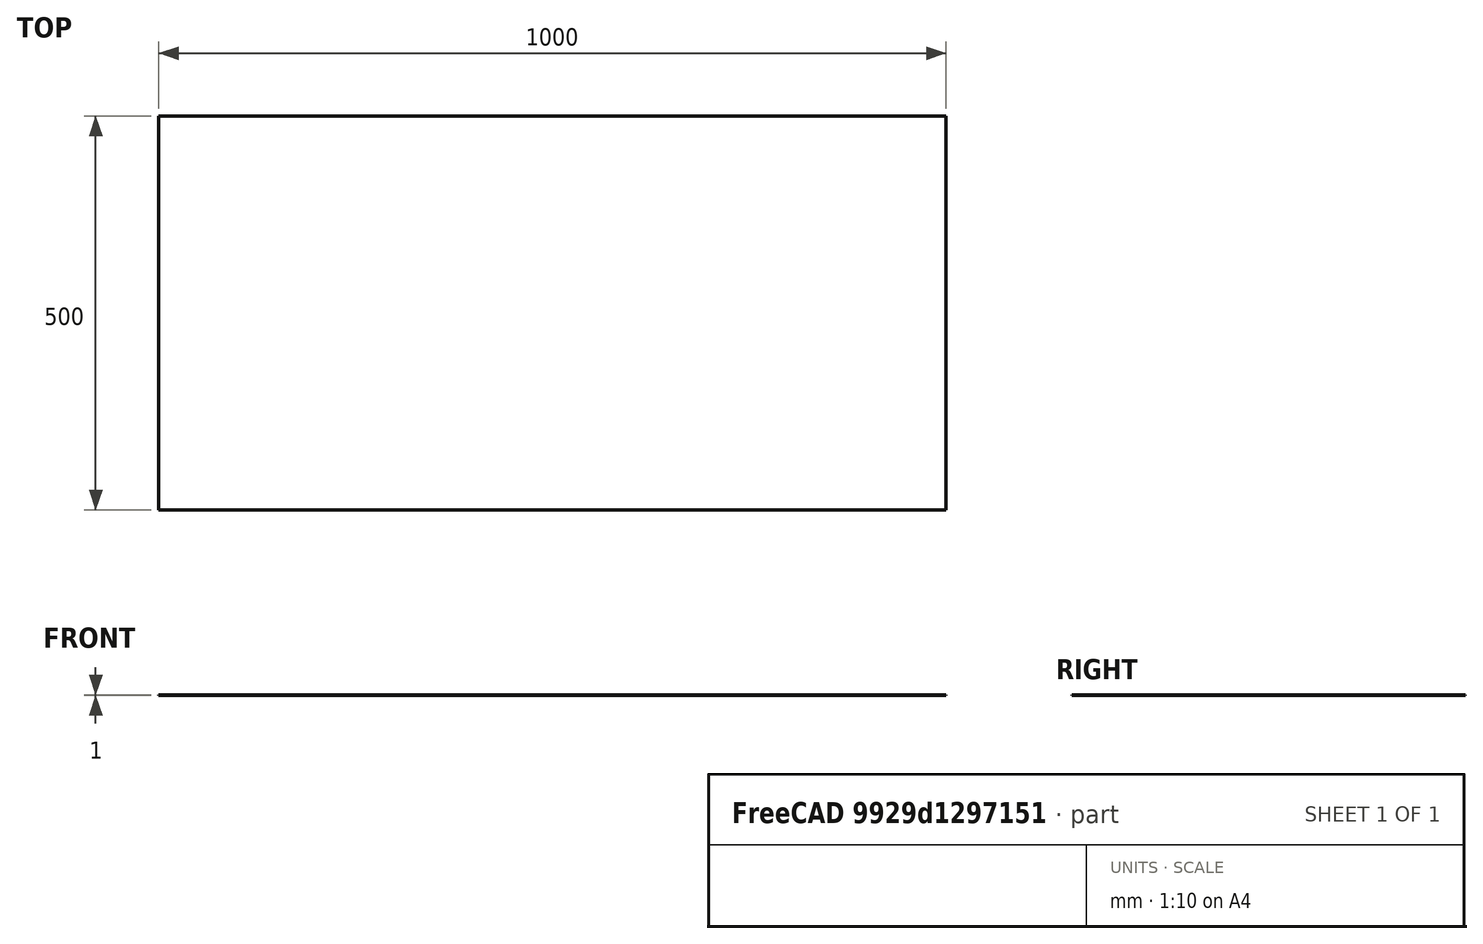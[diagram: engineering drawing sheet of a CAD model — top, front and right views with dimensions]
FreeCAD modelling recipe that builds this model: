
FCSTD DOCUMENT  (FreeCAD 0.18R16131 (Git))
Label: fond_caisse
License: All rights reserved
LicenseURL: http://en.wikipedia.org/wiki/All_rights_reserved
objects: Sketcher::SketchObject×3, Spreadsheet::Sheet×1, PartDesign::Pad×1, PartDesign::Body×1
note: 6 computed .brp shape members not serialized (recipe doc carries the construction recipe); baked Part::Feature solids carry a one-line shape summary decoded from their .brp

FEATURE [Sketcher::SketchObject] Sketch  label="fond_caisse"
  Placement = pos=(0,0,0) rot=(-1,0,0;3.14159rad)
  sketch-geometry (4):
    g0: LineSegment StartX=-717.714 StartY=524.52 StartZ=0 EndX=282.286 EndY=524.52 EndZ=0
    g1: LineSegment StartX=282.286 StartY=524.52 StartZ=0 EndX=282.286 EndY=24.52 EndZ=0
    g2: LineSegment StartX=282.286 StartY=24.52 StartZ=0 EndX=-717.714 EndY=24.52 EndZ=0
    g3: LineSegment StartX=-717.714 StartY=24.52 StartZ=0 EndX=-717.714 EndY=524.52 EndZ=0
  constraints (10):
    c: Coincident(g0,g1)
    c: Coincident(g1,g2)
    c: Coincident(g2,g3)
    c: Coincident(g3,g0)
    c: Horizontal(g0)
    c: Horizontal(g2)
    c: Vertical(g1)
    c: Vertical(g3)
    c: DistanceX(g0,g0) = 1000
    c: DistanceY(g1,g1) = 500
FEATURE [Spreadsheet::Sheet] Spreadsheet  label="dimensions_caisse"
  cells = A1=Longueur caisse (mm); B1=Largeur caisse (mm); C1=Epaisseur parois (mm=; A2(longueur_caisse)==1000mm; B2(largeur_caisse)==500mm; C2(epaisseur_caisse)==30mm
FEATURE [Sketcher::SketchObject] Sketch001  label="fond_caisse001"
  Placement = pos=(0,0,0) rot=(1,0,0;3.14159rad)
  sketch-geometry (4):
    g0: LineSegment StartX=-717.714 StartY=524.52 StartZ=0 EndX=282.286 EndY=524.52 EndZ=0
    g1: LineSegment StartX=282.286 StartY=524.52 StartZ=0 EndX=282.286 EndY=24.52 EndZ=0
    g2: LineSegment StartX=282.286 StartY=24.52 StartZ=0 EndX=-717.714 EndY=24.52 EndZ=0
    g3: LineSegment StartX=-717.714 StartY=24.52 StartZ=0 EndX=-717.714 EndY=524.52 EndZ=0
  constraints (10):
    c: Coincident(g0,g1)
    c: Coincident(g1,g2)
    c: Coincident(g2,g3)
    c: Coincident(g3,g0)
    c: Horizontal(g0)
    c: Horizontal(g2)
    c: Vertical(g1)
    c: Vertical(g3)
    c: DistanceX(g0,g0) = 1000
    c: DistanceY(g1,g1) = 500
FEATURE [Sketcher::SketchObject] CopySketch001
  Placement = pos=(0,0,0) rot=(1,0,0;3.14159rad)
  sketch-geometry (4):
    g0: LineSegment StartX=-717.714 StartY=524.52 StartZ=0 EndX=282.286 EndY=524.52 EndZ=0
    g1: LineSegment StartX=282.286 StartY=524.52 StartZ=0 EndX=282.286 EndY=24.52 EndZ=0
    g2: LineSegment StartX=282.286 StartY=24.52 StartZ=0 EndX=-717.714 EndY=24.52 EndZ=0
    g3: LineSegment StartX=-717.714 StartY=24.52 StartZ=0 EndX=-717.714 EndY=524.52 EndZ=0
  constraints (10):
    c: Coincident(g0,g1)
    c: Coincident(g1,g2)
    c: Coincident(g2,g3)
    c: Coincident(g3,g0)
    c: Horizontal(g0)
    c: Horizontal(g2)
    c: Vertical(g1)
    c: Vertical(g3)
    c: DistanceX(g0,g0) = 1000
    c: DistanceY(g1,g1) = 500
FEATURE [PartDesign::Pad] Pad
  Length = 1
  Length2 = 100
  Placement = pos=(0,0,0) rot=(1,0,0;3.14159rad)
  Profile = -> CopySketch001
  Type = 0
FEATURE [PartDesign::Body] Body  label="body_fond_caisse"
  Group = -> [Pad]
  Origin = -> Origin
  Tip = -> Pad
